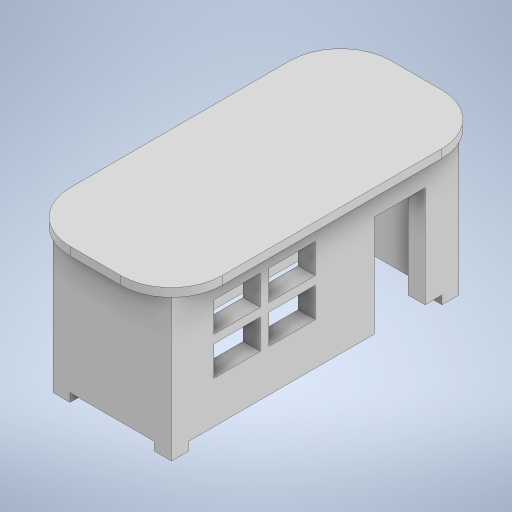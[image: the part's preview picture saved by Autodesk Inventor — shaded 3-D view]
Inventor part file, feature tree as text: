
AUTODESK INVENTOR PART (.ipt)
format: ipt  version: 2023 (Build 270158000, 158)  size: 301,568 bytes
history: native  units: mm
features: extrude x4, sketch x4, fillet x1
ambient origin geometry x8: Origin, YZ Plane, XZ Plane, XY Plane, X Axis, Y Axis, Z Axis, Center Point
bodies: Solid1 (feature_tree)
feature tree (9):
  extrude  "Extrusion1"  Depth=10.0mm
  extrude  "Extrusion2"  Depth=10.0mm
  extrude  "Extrusion3"  Depth=10.0mm
  fillet  "Fillet1"  Radius=150.0mm
  extrude  "Extrusion4"  Depth=5.0mm TaperAngle=0.0deg
  sketch  "Sketch1"  dims[d0=10.0mm d1=10.0mm]
  sketch  "Sketch2"  dims[d2=10.0mm d3=10.0mm]
  sketch  "Sketch3"  dims[d4=10.0mm d5=10.0mm d6=150.0mm]
  sketch  "Sketch4"  dims[d7=50.0mm d8=5.0mm d9=0.0mm d10=80.0mm d11=0.0mm d12=10.0mm d13=10.0mm d14=10.0mm d15=10.0mm d16=5.0mm d17=0.0mm d18=30.0mm d19=60.0mm d20=30.0mm d21=40.0mm d22=60.0mm d23=25.0mm d24=20.0mm d25=0.0mm d26=15.0mm d27=5.0mm d28=5.0mm d29=17.5mm d30=27.5mm d31=10.0mm d32=0.0mm]
